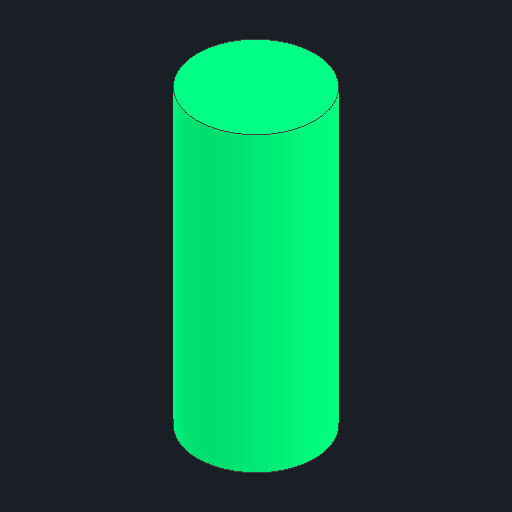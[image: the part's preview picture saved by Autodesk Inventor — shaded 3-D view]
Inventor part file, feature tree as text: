
AUTODESK INVENTOR PART (.ipt)
format: ipt  version: 2025.2 (Build 292293000, 293)  size: 83,456 bytes
history: native  units: in
note: dims shown in document units (in); Inventor stores cm internally (conversion verified against a paired STEP export)
features: other x3, sketch x1
ambient origin geometry x8: Origin, YZ Plane, XZ Plane, XY Plane, X Axis, Y Axis, Z Axis, Center Point
bodies: Solid1 (feature_tree)
feature tree (4):
  other  "26650(Green)_MIR_MIR.ipt"
  other  "Solid1::26650(Green)_MIR_MIR.ipt"
  other  "TaggingFeature1"
  sketch  "Sketch1"  dims[d0=0.3937in]
